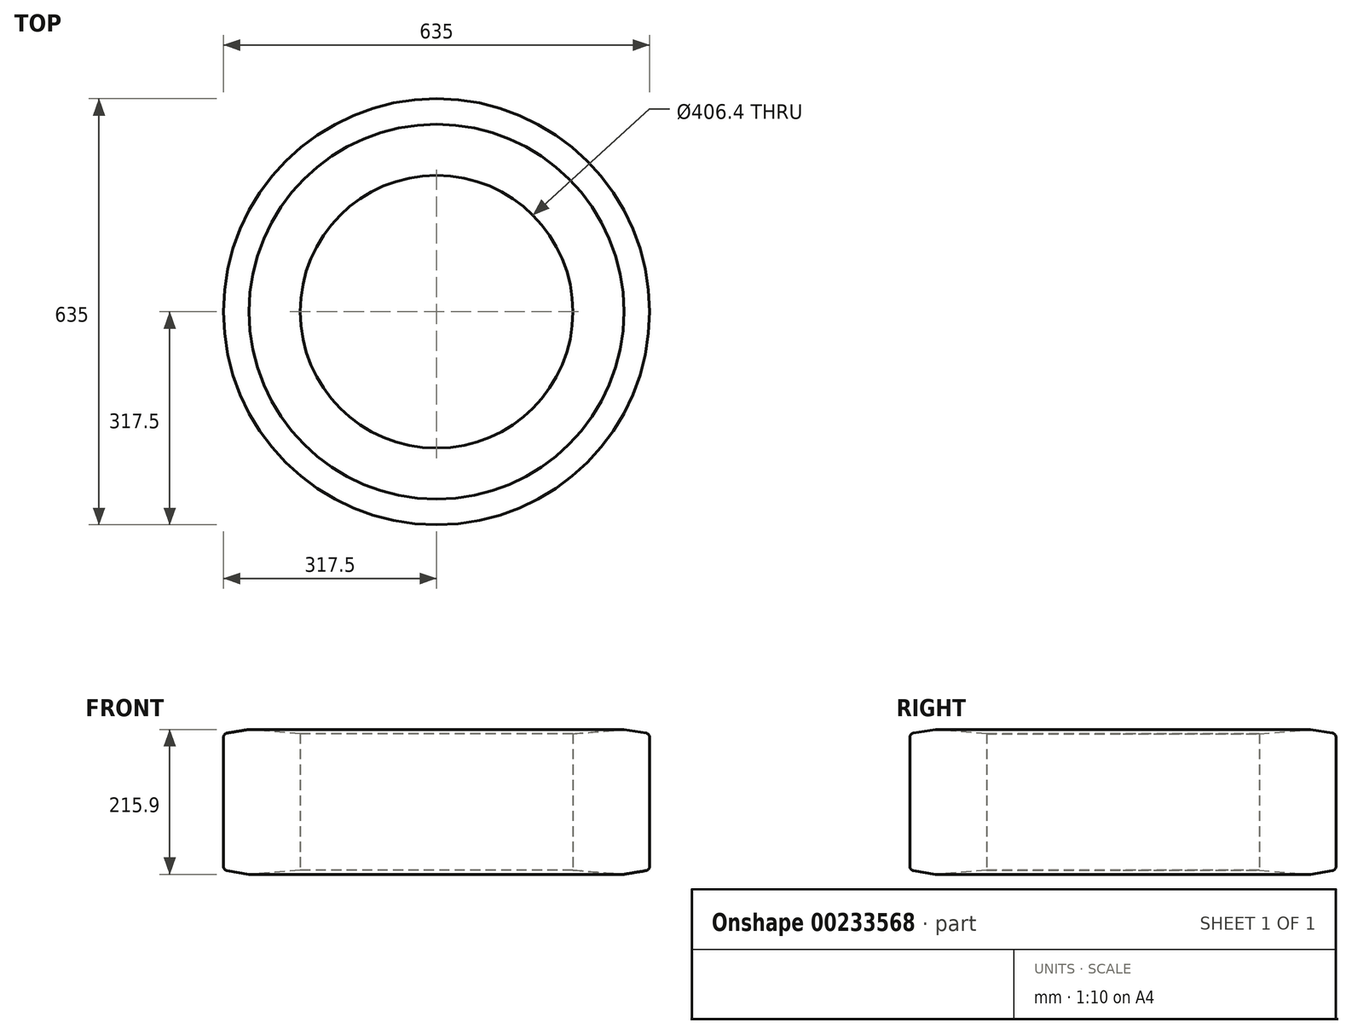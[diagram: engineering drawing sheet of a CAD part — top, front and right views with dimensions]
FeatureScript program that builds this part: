
annotation { "Feature Type Name" : "Feature", "Feature Type Description" : "" }
export const myFeature = defineFeature(function(context is Context, id is Id, definition is map)
    precondition{}
    {
        {
            var Q0;
            Q0=qCreatedBy(makeId("Top.planeOp"),FACE);
            var sketch = newSketch(context, id + "F0", { "sketchPlane" : qUnion([Q0])});
            skCircle(sketch, "E0", {"center": v(0, 0) * mm, "radius": 317.5 * mm});
            skCircle(sketch, "E1", {"center": v(0, 0) * mm, "radius": 203.2 * mm});
            skLineSegment(sketch, "E2", {"start": v(0, 0) * mm, "end": v(0, 317.5) * mm});
            skSolve(sketch);
        }
        {
            var Q0;
            Q0=qSketchRegion(id+"F0",true);
            extrude(context, id + "F1", {"entities" : qUnion([Q0]), "depth" : 209.55 * mm, "hasSecondDirection" : true, "secondDirectionOppositeDirection" : true, "secondDirectionDepth" : 6.35 * mm});
        }
        {
            var Q0;
            Q0=makeQuery(id+"F1.opExtrude","CAP_EDGE",EDGE,{"disambiguationData":[OSD([sQuery(id+"F0.wireOp",EDGE,"E0")])],"isStart":true});
            chamfer(context, id + "F2", {"entities" : qUnion([Q0]), "chamferType" : ChamferType.TWO_OFFSETS, "width1" : 6.35 * mm, "oppositeDirection" : false, "width2" : 38.1 * mm, "tangentPropagation" : true});
        }
        {
            var Q0;
            Q0=makeQuery(id+"F1.opExtrude","CAP_EDGE",EDGE,{"disambiguationData":[OSD([sQuery(id+"F0.wireOp",EDGE,"E0")])],"isStart":false});
            chamfer(context, id + "F3", {"entities" : qUnion([Q0]), "chamferType" : ChamferType.TWO_OFFSETS, "width1" : 6.35 * mm, "oppositeDirection" : true, "width2" : 38.1 * mm, "tangentPropagation" : true});
        }
        {
            var Q0;
            Q0=makeQuery(id+"F1.opExtrude","CAP_EDGE",EDGE,{"disambiguationData":[OSD([sQuery(id+"F0.wireOp",EDGE,"E1")])],"isStart":true});
            chamfer(context, id + "F4", {"entities" : qUnion([Q0]), "chamferType" : ChamferType.TWO_OFFSETS, "width1" : 76.2 * mm, "oppositeDirection" : false, "width2" : 6.35 * mm, "tangentPropagation" : true});
        }
        {
            var Q0;
            Q0=makeQuery(id+"F1.opExtrude","CAP_EDGE",EDGE,{"disambiguationData":[OSD([sQuery(id+"F0.wireOp",EDGE,"E1")])],"isStart":false});
            chamfer(context, id + "F5", {"entities" : qUnion([Q0]), "chamferType" : ChamferType.TWO_OFFSETS, "width1" : 6.35 * mm, "oppositeDirection" : false, "width2" : 76.2 * mm, "tangentPropagation" : true});
        }
        {
            var Q0;
            {var subQ0=sQuery(id+"F0.wireOp",EDGE,"E0");Q0=makeQuery(id+"F2.opChamfer","BLEND_EDGE",EDGE,{"blendedFrom":[makeQuery(id+"F1.opExtrude","CAP_EDGE",EDGE,{"disambiguationData":[OSD([subQ0])],"isStart":true}),makeQuery(id+"F1.opExtrude","SWEPT_FACE",FACE,{"disambiguationData":[OSD([subQ0])]})],"blendedInto":[makeQuery(id+"F1.opExtrude","SWEPT_FACE",FACE,{"disambiguationData":[OSD([subQ0])]})]});}
            var Q1;
            {var subQ0=sQuery(id+"F0.wireOp",EDGE,"E0");Q1=makeQuery(id+"F3.opChamfer","BLEND_EDGE",EDGE,{"blendedFrom":[makeQuery(id+"F1.opExtrude","CAP_EDGE",EDGE,{"disambiguationData":[OSD([subQ0])],"isStart":false}),makeQuery(id+"F1.opExtrude","SWEPT_FACE",FACE,{"disambiguationData":[OSD([subQ0])]})],"blendedInto":[makeQuery(id+"F1.opExtrude","SWEPT_FACE",FACE,{"disambiguationData":[OSD([subQ0])]})]});}
            fillet(context, id + "F6", {"entities" : qUnion([Q0, Q1]), "radius" : 6.35 * mm, "tangentPropagation" : true, "allowEdgeOverflow" : false});
        }
    });
